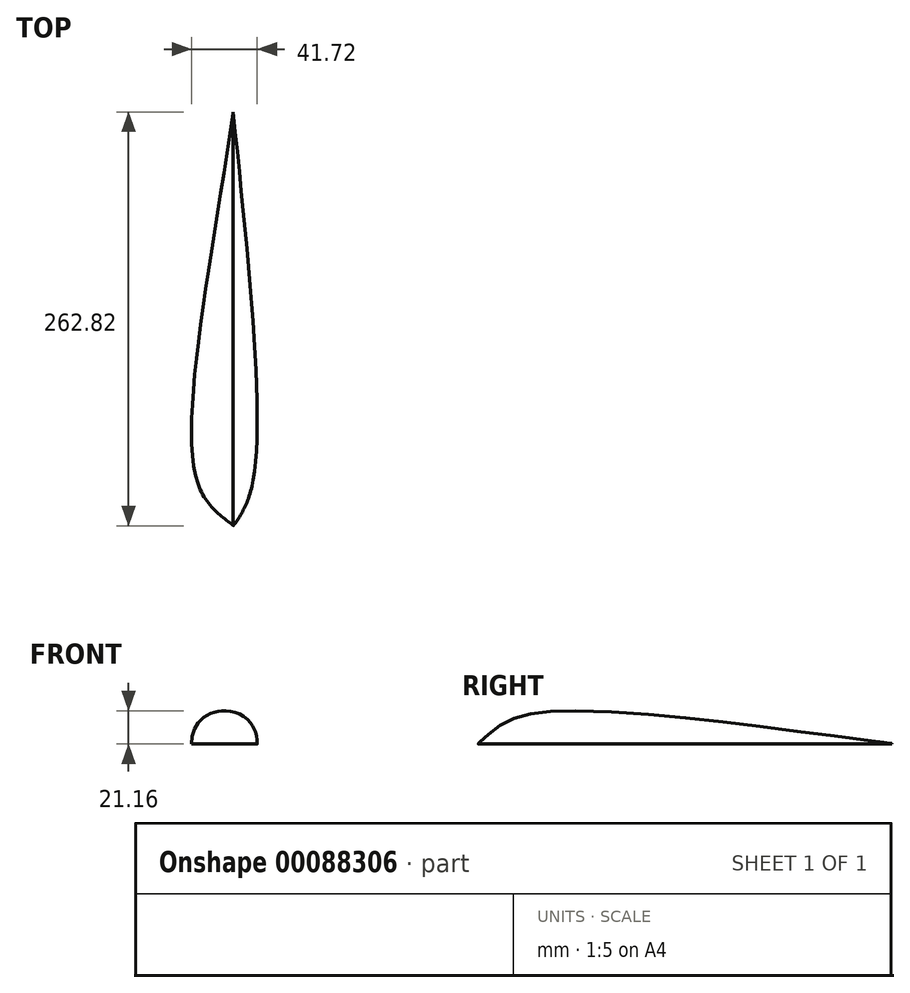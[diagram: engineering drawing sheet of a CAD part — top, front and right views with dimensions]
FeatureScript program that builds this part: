
annotation { "Feature Type Name" : "Feature", "Feature Type Description" : "" }
export const myFeature = defineFeature(function(context is Context, id is Id, definition is map)
    precondition{}
    {
        {
            var Q0;
            Q0=qCreatedBy(makeId("Top.planeOp"),FACE);
            var sketch = newSketch(context, id + "F0", { "sketchPlane" : qUnion([Q0])});
            skLineSegment(sketch, "E0", {"start": v(0, -143.15) * mm, "end": v(0, 210.72) * mm, "construction": true});
            skSolve(sketch);
        }
        {
            var Q0;
            Q0=sQuery(id+"F0.wireOp",EDGE,"E0");
            cPlane(context, id + "F1", {"entities" : qUnion([Q0]), "cplaneType" : CPlaneType.LINE_ANGLE, "offset" : 150 * mm, "angle" : 0.1 * degree, "width" : 150 * mm, "height" : 150 * mm});
        }
        {
            var Q0;
            Q0=qCreatedBy(makeId("Top.planeOp"),FACE);
            var sketch = newSketch(context, id + "F2", { "sketchPlane" : qUnion([Q0])});
            skFitSpline(sketch, "E1", {"points": [v(0, -96) * mm, v(12.73, -66.98) * mm, v(0, 166.8) * mm], "startDerivative": vector(56.05, 79.43) * mm, "endDerivative": vector(-41.09, 397.25) * mm});
            skLineSegment(sketch, "E2", {"start": v(0, -96) * mm, "end": v(0, 166.8) * mm});
            skSolve(sketch);
        }
        {
            var Q0;
            Q0=qCreatedBy(id+"F1.planeOp",FACE);
            var sketch = newSketch(context, id + "F3", { "sketchPlane" : qUnion([Q0])});
            skLineSegment(sketch, "E3", {"start": v(-0.16, -95.8) * mm, "end": v(-0.16, 166) * mm});
            skFitSpline(sketch, "E4", {"points": [v(-0.16, -95.8) * mm, v(-22.45, -69.3) * mm, v(-0.16, 166) * mm], "startDerivative": vector(-80.52, 67.95) * mm, "endDerivative": vector(59.1, 404.05) * mm});
            skSolve(sketch);
        }
        {
            var Q0;
            Q0=qSketchRegion(id+"F3",true);
            var Q1;
            Q1=qSketchRegion(id+"F2",true);
            var Q2;
            Q2=sQuery(id+"F3.wireOp",VERTEX,"E4.1.internal");
            var Q3;
            Q3=sQuery(id+"F2.wireOp",VERTEX,"E1.1.internal");
            loft(context, id + "F4", {"startCondition" : LoftEndDerivativeType.NORMAL_TO_PROFILE, "startMagnitude" : 20, "endCondition" : LoftEndDerivativeType.NORMAL_TO_PROFILE, "endMagnitude" : 20, "sheetProfilesArray" : [{ "sheetProfileEntities" : qUnion([Q0]) }, { "sheetProfileEntities" : qUnion([Q1]) }], "matchConnections" : true, "connections" : [{ "connectionEntities" : qUnion([Q2, Q3]), "connectionEdgeQueries" : qUnion([]), "connectionEdgeParameters" : [] }]});
        }
    });
